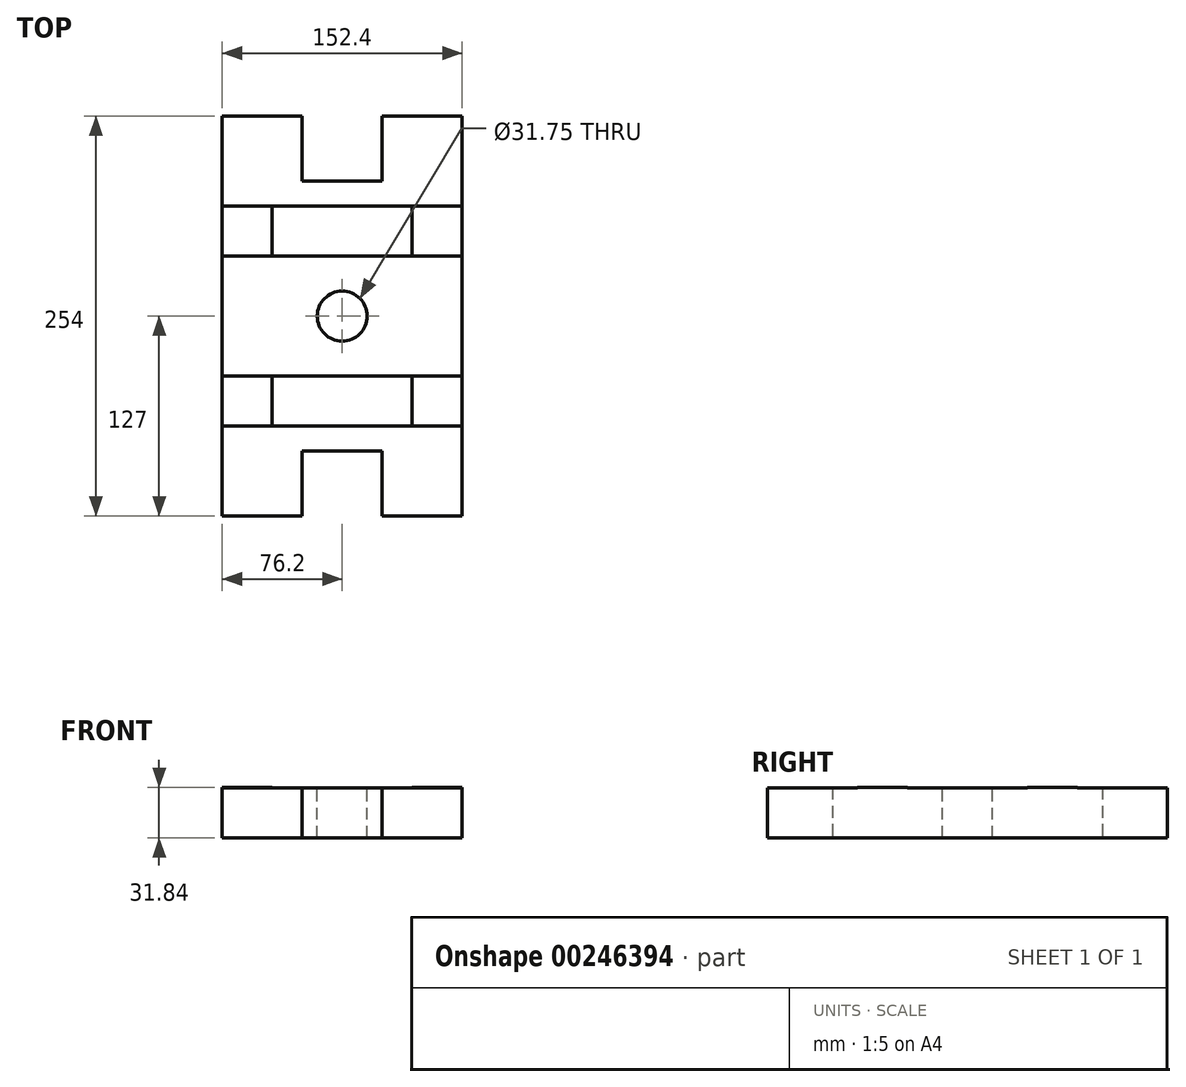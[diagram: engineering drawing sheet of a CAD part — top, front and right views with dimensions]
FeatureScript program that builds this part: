
annotation { "Feature Type Name" : "Feature", "Feature Type Description" : "" }
export const myFeature = defineFeature(function(context is Context, id is Id, definition is map)
    precondition{}
    {
        {
            var Q0;
            Q0=qCreatedBy(makeId("Top.planeOp"),FACE);
            var sketch = newSketch(context, id + "F0", { "sketchPlane" : qUnion([Q0])});
            skLineSegment(sketch, "E0", {"start": v(0, 0) * mm, "end": v(-76.2, 0) * mm, "construction": true});
            skLineSegment(sketch, "E1", {"start": v(0, 0) * mm, "end": v(76.2, 0) * mm, "construction": true});
            skLineSegment(sketch, "E2", {"start": v(-76.2, 0) * mm, "end": v(-76.2, 127) * mm});
            skLineSegment(sketch, "E3", {"start": v(-76.2, 0) * mm, "end": v(-76.2, -127) * mm});
            skLineSegment(sketch, "E4", {"start": v(-76.2, 127) * mm, "end": v(-25.4, 127) * mm});
            skLineSegment(sketch, "E5", {"start": v(-25.4, 127) * mm, "end": v(-25.4, 85.72) * mm});
            skLineSegment(sketch, "E6", {"start": v(-25.4, 85.73) * mm, "end": v(25.4, 85.73) * mm});
            skLineSegment(sketch, "E7", {"start": v(25.4, 85.73) * mm, "end": v(25.4, 127) * mm});
            skLineSegment(sketch, "E8", {"start": v(76.2, 0) * mm, "end": v(76.2, 127) * mm});
            skLineSegment(sketch, "E9", {"start": v(76.2, 0) * mm, "end": v(76.2, -127) * mm});
            skLineSegment(sketch, "E10", {"start": v(76.2, 127) * mm, "end": v(25.4, 127) * mm});
            skLineSegment(sketch, "E11", {"start": v(-76.2, -127) * mm, "end": v(-25.4, -127) * mm});
            skLineSegment(sketch, "E12", {"start": v(-25.4, -127) * mm, "end": v(-25.4, -85.72) * mm});
            skLineSegment(sketch, "E13", {"start": v(-25.4, -85.72) * mm, "end": v(25.4, -85.72) * mm});
            skLineSegment(sketch, "E14", {"start": v(25.4, -85.72) * mm, "end": v(25.4, -127) * mm});
            skLineSegment(sketch, "E15", {"start": v(76.2, -127) * mm, "end": v(25.4, -127) * mm});
            skSolve(sketch);
        }
        {
            var Q0;
            Q0=makeQuery(id+"F0.imprint","IMPRINT",FACE,{"disambiguationData":[TD([[makeQuery(id+"F0.imprint","IMPRINT",EDGE,{"derivedFrom":sQuery(id+"F0.wireOp",EDGE,"E2")}),-1.0]])]});
            extrude(context, id + "F1", {"entities" : qUnion([Q0]), "depth" : 31.75 * mm});
        }
        {
            var Q0;
            Q0=makeQuery(id+"F1.opExtrude","CAP_FACE",FACE,{"disambiguationData":[OSD([sQuery(id+"F0.wireOp",EDGE,"E2"),sQuery(id+"F0.wireOp",EDGE,"E3"),sQuery(id+"F0.wireOp",EDGE,"E4"),sQuery(id+"F0.wireOp",EDGE,"E5"),sQuery(id+"F0.wireOp",EDGE,"E6"),sQuery(id+"F0.wireOp",EDGE,"E7"),sQuery(id+"F0.wireOp",EDGE,"E8"),sQuery(id+"F0.wireOp",EDGE,"E9"),sQuery(id+"F0.wireOp",EDGE,"E10"),sQuery(id+"F0.wireOp",EDGE,"E11"),sQuery(id+"F0.wireOp",EDGE,"E12"),sQuery(id+"F0.wireOp",EDGE,"E13"),sQuery(id+"F0.wireOp",EDGE,"E14"),sQuery(id+"F0.wireOp",EDGE,"E15")])],"isStart":false});
            var sketch = newSketch(context, id + "F2", { "sketchPlane" : qUnion([Q0])});
            skLineSegment(sketch, "E16", {"start": v(-76.2, -127) * mm, "end": v(-76.2, -69.85) * mm, "construction": true});
            skLineSegment(sketch, "E17", {"start": v(-76.2, -69.85) * mm, "end": v(-76.2, 69.85) * mm});
            skLineSegment(sketch, "E18", {"start": v(-76.2, -69.85) * mm, "end": v(76.2, -69.85) * mm});
            skLineSegment(sketch, "E19", {"start": v(-76.2, 69.85) * mm, "end": v(76.2, 69.85) * mm});
            skLineSegment(sketch, "E20", {"start": v(76.2, 69.85) * mm, "end": v(76.2, -69.85) * mm});
            skSolve(sketch);
        }
        {
            var Q0;
            Q0=makeQuery(id+"F2.imprint","IMPRINT",FACE,{"disambiguationData":[TD([[makeQuery(id+"F2.imprint","IMPRINT",EDGE,{"derivedFrom":sQuery(id+"F2.wireOp",EDGE,"E17")}),-1.0]])]});
            extrude(context, id + "F3", {"entities" : qUnion([Q0]), "operationType" : NewBodyOperationType.ADD, "depth" : 7 / 203.2 * mm});
        }
        {
            var Q0;
            Q0=makeQuery(id+"F3.opExtrude","CAP_FACE",FACE,{"disambiguationData":[OSD([sQuery(id+"F2.wireOp",EDGE,"E17"),sQuery(id+"F2.wireOp",EDGE,"E18"),sQuery(id+"F2.wireOp",EDGE,"E19"),sQuery(id+"F2.wireOp",EDGE,"E20")])],"isStart":false});
            var sketch = newSketch(context, id + "F4", { "sketchPlane" : qUnion([Q0])});
            skLineSegment(sketch, "E21", {"start": v(-76.2, 69.85) * mm, "end": v(-76.2, 38.1) * mm});
            skLineSegment(sketch, "E22", {"start": v(-76.2, -69.85) * mm, "end": v(-76.2, -38.1) * mm});
            skLineSegment(sketch, "E23", {"start": v(-76.2, 69.85) * mm, "end": v(76.2, 69.85) * mm});
            skLineSegment(sketch, "E24", {"start": v(76.2, 69.85) * mm, "end": v(76.2, 38.1) * mm});
            skLineSegment(sketch, "E25", {"start": v(-76.2, 38.1) * mm, "end": v(76.2, 38.1) * mm});
            skLineSegment(sketch, "E26", {"start": v(-76.2, -38.1) * mm, "end": v(76.2, -38.1) * mm});
            skLineSegment(sketch, "E27", {"start": v(76.2, -38.1) * mm, "end": v(76.2, -69.85) * mm});
            skLineSegment(sketch, "E28", {"start": v(76.2, -69.85) * mm, "end": v(-76.2, -69.85) * mm});
            skSolve(sketch);
        }
        {
            var Q0;
            Q0=makeQuery(id+"F4.imprint","IMPRINT",FACE,{"disambiguationData":[TD([[makeQuery(id+"F4.imprint","IMPRINT",EDGE,{"derivedFrom":sQuery(id+"F4.wireOp",EDGE,"E21")}),-1.0]])]});
            var Q1;
            Q1=makeQuery(id+"F4.imprint","IMPRINT",FACE,{"disambiguationData":[TD([[makeQuery(id+"F4.imprint","IMPRINT",EDGE,{"derivedFrom":sQuery(id+"F4.wireOp",EDGE,"E22")}),-1.0]])]});
            extrude(context, id + "F5", {"entities" : qUnion([Q0, Q1]), "operationType" : NewBodyOperationType.ADD, "depth" : 3 / 101.6 * mm});
        }
        {
            var Q0;
            Q0=makeQuery(id+"F5.opExtrude","CAP_FACE",FACE,{"disambiguationData":[OSD([sQuery(id+"F4.wireOp",EDGE,"E21"),sQuery(id+"F4.wireOp",EDGE,"E23"),sQuery(id+"F4.wireOp",EDGE,"E24"),sQuery(id+"F4.wireOp",EDGE,"E25")])],"isStart":false});
            var sketch = newSketch(context, id + "F6", { "sketchPlane" : qUnion([Q0])});
            skLineSegment(sketch, "E29", {"start": v(-76.2, 69.85) * mm, "end": v(-76.2, 38.1) * mm});
            skLineSegment(sketch, "E30", {"start": v(-76.2, 38.1) * mm, "end": v(-44.45, 38.1) * mm});
            skLineSegment(sketch, "E31", {"start": v(-44.45, 38.1) * mm, "end": v(-44.45, 69.85) * mm});
            skLineSegment(sketch, "E32", {"start": v(-44.45, 69.85) * mm, "end": v(-76.2, 69.85) * mm});
            skLineSegment(sketch, "E33", {"start": v(76.2, 69.85) * mm, "end": v(76.2, 38.1) * mm});
            skLineSegment(sketch, "E34", {"start": v(76.2, 38.1) * mm, "end": v(44.45, 38.1) * mm});
            skLineSegment(sketch, "E35", {"start": v(44.45, 38.1) * mm, "end": v(44.45, 69.85) * mm});
            skLineSegment(sketch, "E36", {"start": v(44.45, 69.85) * mm, "end": v(76.2, 69.85) * mm});
            skSolve(sketch);
        }
        {
            var Q0;
            Q0=makeQuery(id+"F6.imprint","IMPRINT",FACE,{"disambiguationData":[TD([[makeQuery(id+"F6.imprint","IMPRINT",EDGE,{"derivedFrom":sQuery(id+"F6.wireOp",EDGE,"E29")}),-1.0]])]});
            var Q1;
            Q1=makeQuery(id+"F6.imprint","IMPRINT",FACE,{"disambiguationData":[TD([[makeQuery(id+"F6.imprint","IMPRINT",EDGE,{"derivedFrom":sQuery(id+"F6.wireOp",EDGE,"E33")}),-1.0]])]});
            extrude(context, id + "F7", {"entities" : qUnion([Q0, Q1]), "operationType" : NewBodyOperationType.ADD, "depth" : 3 / 101.6 * mm});
        }
        {
            var Q0;
            Q0=makeQuery(id+"F5.opExtrude","CAP_FACE",FACE,{"disambiguationData":[OSD([sQuery(id+"F4.wireOp",EDGE,"E22"),sQuery(id+"F4.wireOp",EDGE,"E26"),sQuery(id+"F4.wireOp",EDGE,"E27"),sQuery(id+"F4.wireOp",EDGE,"E28")])],"isStart":false});
            var sketch = newSketch(context, id + "F8", { "sketchPlane" : qUnion([Q0])});
            skLineSegment(sketch, "E37", {"start": v(-76.2, -38.1) * mm, "end": v(-76.2, -69.85) * mm});
            skLineSegment(sketch, "E38", {"start": v(-76.2, -69.85) * mm, "end": v(-44.45, -69.85) * mm});
            skLineSegment(sketch, "E39", {"start": v(-44.45, -69.85) * mm, "end": v(-44.45, -38.1) * mm});
            skLineSegment(sketch, "E40", {"start": v(-44.45, -38.1) * mm, "end": v(-76.2, -38.1) * mm});
            skLineSegment(sketch, "E41", {"start": v(76.2, -38.1) * mm, "end": v(76.2, -69.85) * mm});
            skLineSegment(sketch, "E42", {"start": v(76.2, -69.85) * mm, "end": v(44.45, -69.85) * mm});
            skLineSegment(sketch, "E43", {"start": v(44.45, -69.85) * mm, "end": v(44.45, -38.1) * mm});
            skLineSegment(sketch, "E44", {"start": v(76.2, -38.1) * mm, "end": v(44.45, -38.1) * mm});
            skSolve(sketch);
        }
        {
            var Q0;
            Q0=makeQuery(id+"F8.imprint","IMPRINT",FACE,{"disambiguationData":[TD([[makeQuery(id+"F8.imprint","IMPRINT",EDGE,{"derivedFrom":sQuery(id+"F8.wireOp",EDGE,"E37")}),-1.0]])]});
            var Q1;
            Q1=makeQuery(id+"F8.imprint","IMPRINT",FACE,{"disambiguationData":[TD([[makeQuery(id+"F8.imprint","IMPRINT",EDGE,{"derivedFrom":sQuery(id+"F8.wireOp",EDGE,"E41")}),-1.0]])]});
            extrude(context, id + "F9", {"entities" : qUnion([Q0, Q1]), "operationType" : NewBodyOperationType.ADD, "depth" : 3 / 101.6 * mm});
        }
        {
            var Q0;
            Q0=makeQuery(id+"F3.opExtrude","CAP_FACE",FACE,{"disambiguationData":[OSD([sQuery(id+"F2.wireOp",EDGE,"E17"),sQuery(id+"F2.wireOp",EDGE,"E18"),sQuery(id+"F2.wireOp",EDGE,"E19"),sQuery(id+"F2.wireOp",EDGE,"E20")])],"isStart":false});
            var sketch = newSketch(context, id + "F10", { "sketchPlane" : qUnion([Q0])});
            skPoint(sketch, "E45", {"position": v(0, 0) * mm});
            skSolve(sketch);
        }
        {
            var Q0;
            Q0=sQuery(id+"F10.wireOp",VERTEX,"E45");
            var Q1;
            Q1=makeQuery(id+"F1.opExtrude","SWEPT_BODY",BODY,{"disambiguationData":[OSD([sQuery(id+"F0.wireOp",EDGE,"E2"),sQuery(id+"F0.wireOp",EDGE,"E3"),sQuery(id+"F0.wireOp",EDGE,"E4"),sQuery(id+"F0.wireOp",EDGE,"E5"),sQuery(id+"F0.wireOp",EDGE,"E6"),sQuery(id+"F0.wireOp",EDGE,"E7"),sQuery(id+"F0.wireOp",EDGE,"E8"),sQuery(id+"F0.wireOp",EDGE,"E9"),sQuery(id+"F0.wireOp",EDGE,"E10"),sQuery(id+"F0.wireOp",EDGE,"E11"),sQuery(id+"F0.wireOp",EDGE,"E12"),sQuery(id+"F0.wireOp",EDGE,"E13"),sQuery(id+"F0.wireOp",EDGE,"E14"),sQuery(id+"F0.wireOp",EDGE,"E15")])]});
            hole(context, id + "F11", {"style" : HoleStyle.SIMPLE, "endStyle" : HoleEndStyle.THROUGH, "holeDiameter" : 31.75 * mm, "tappedDepth" : 12.7 * mm, "tapClearance" : 3, "locations" : qUnion([Q0]), "scope" : qUnion([Q1])});
        }
    });
